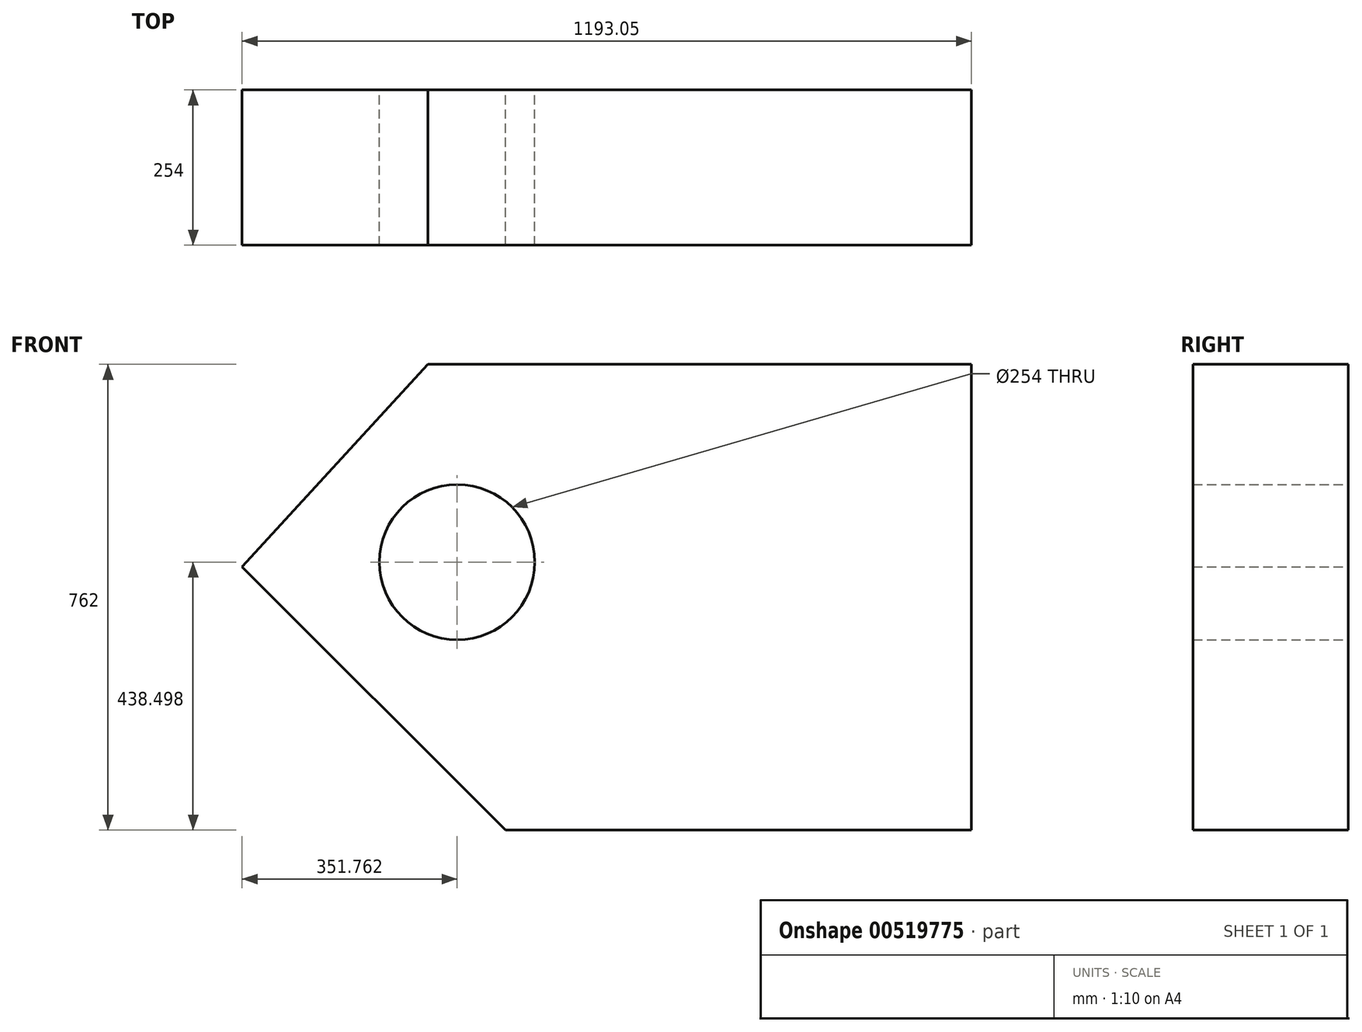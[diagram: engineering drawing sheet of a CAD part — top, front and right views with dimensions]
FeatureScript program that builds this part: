
annotation { "Feature Type Name" : "Feature", "Feature Type Description" : "" }
export const myFeature = defineFeature(function(context is Context, id is Id, definition is map)
    precondition{}
    {
        {
            var Q0;
            Q0=qCreatedBy(makeId("Front.planeOp"),FACE);
            var sketch = newSketch(context, id + "F0", { "sketchPlane" : qUnion([Q0])});
            skLineSegment(sketch, "E0", {"start": v(0, 0) * mm, "end": v(762, 0) * mm});
            skLineSegment(sketch, "E1", {"start": v(762, 0) * mm, "end": v(762, 762) * mm});
            skLineSegment(sketch, "E2", {"start": v(762, 762) * mm, "end": v(-127, 762) * mm});
            skLineSegment(sketch, "E3", {"start": v(-127, 762) * mm, "end": v(-431.05, 431.05) * mm});
            skLineSegment(sketch, "E4", {"start": v(-431.05, 431.05) * mm, "end": v(0, 0) * mm});
            skCircle(sketch, "E5", {"center": v(-79.29, 438.5) * mm, "radius": 127 * mm});
            skSolve(sketch);
        }
        {
            var Q0;
            Q0=makeQuery(id+"F0.imprint","IMPRINT",FACE,{"disambiguationData":[TD([[makeQuery(id+"F0.imprint","IMPRINT",EDGE,{"derivedFrom":sQuery(id+"F0.wireOp",EDGE,"E0")}),1.0]])]});
            extrude(context, id + "F1", {"entities" : qUnion([Q0]), "depth" : 254 * mm, "offsetDistance" : 25.4 * mm});
        }
    });
